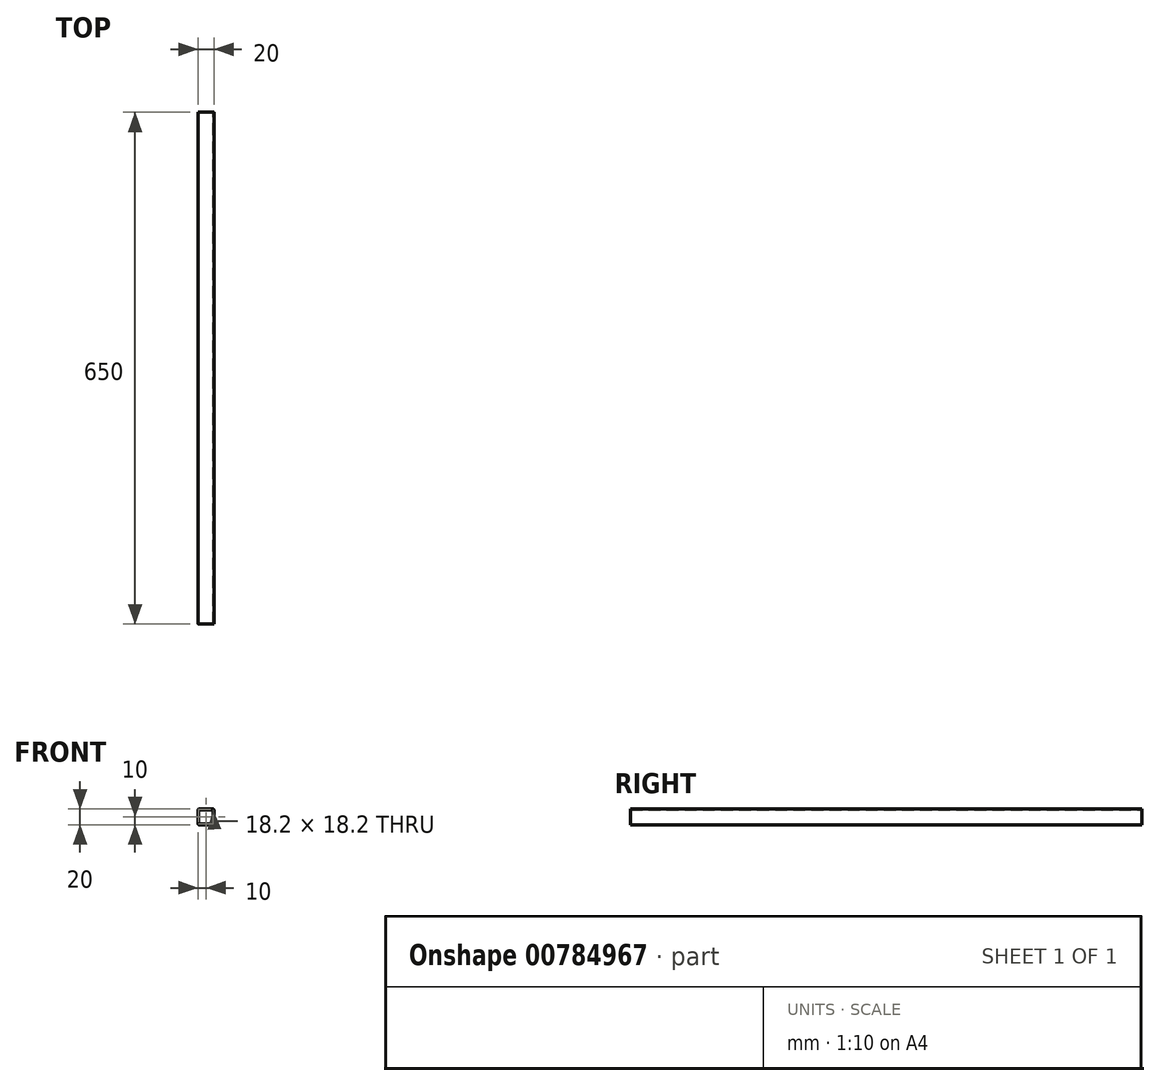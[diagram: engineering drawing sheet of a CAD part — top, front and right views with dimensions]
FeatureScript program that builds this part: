
annotation { "Feature Type Name" : "Feature", "Feature Type Description" : "" }
export const myFeature = defineFeature(function(context is Context, id is Id, definition is map)
    precondition{}
    {
        {
            var Q0;
            Q0=qCreatedBy(makeId("Front.planeOp"),FACE);
            var sketch = newSketch(context, id + "F0", { "sketchPlane" : qUnion([Q0])});
            skLineSegment(sketch, "E0.bottom", {"start": v(-10, 10) * mm, "end": v(10, 10) * mm});
            skLineSegment(sketch, "E0.top", {"start": v(-10, -10) * mm, "end": v(10, -10) * mm});
            skLineSegment(sketch, "E0.left", {"start": v(-10, 10) * mm, "end": v(-10, -10) * mm});
            skLineSegment(sketch, "E0.right", {"start": v(10, 10) * mm, "end": v(10, -10) * mm});
            skPoint(sketch, "E0.middle", {"position": v(0, 0) * mm});
            skLineSegment(sketch, "E1.0", {"start": v(-9.1, 9.1) * mm, "end": v(9.1, 9.1) * mm});
            skLineSegment(sketch, "E1.1", {"start": v(-9.1, 9.1) * mm, "end": v(-9.1, -9.1) * mm});
            skLineSegment(sketch, "E1.2", {"start": v(-9.1, -9.1) * mm, "end": v(9.1, -9.1) * mm});
            skLineSegment(sketch, "E1.3", {"start": v(9.1, 9.1) * mm, "end": v(9.1, -9.1) * mm});
            skSolve(sketch);
        }
        {
            var Q0;
            Q0=makeQuery(id+"F0.imprint","IMPRINT",FACE,{"disambiguationData":[TD([[makeQuery(id+"F0.imprint","IMPRINT",EDGE,{"derivedFrom":sQuery(id+"F0.wireOp",EDGE,"E0.bottom")}),-1.0]])]});
            extrude(context, id + "F1", {"entities" : qUnion([Q0]), "endBound" : BoundingType.SYMMETRIC, "depth" : 650 * mm, "offsetDistance" : 25 * mm});
        }
        {
            var Q0;
            Q0=makeQuery(id+"F1.opExtrude","SWEPT_EDGE",EDGE,{"disambiguationData":[OSD([sQuery(id+"F0.wireOp",EDGE,"E0.bottom"),sQuery(id+"F0.wireOp",EDGE,"E0.right")])]});
            var Q1;
            Q1=makeQuery(id+"F1.opExtrude","SWEPT_EDGE",EDGE,{"disambiguationData":[OSD([sQuery(id+"F0.wireOp",EDGE,"E0.bottom"),sQuery(id+"F0.wireOp",EDGE,"E0.left")])]});
            var Q2;
            Q2=makeQuery(id+"F1.opExtrude","SWEPT_EDGE",EDGE,{"disambiguationData":[OSD([sQuery(id+"F0.wireOp",EDGE,"E0.top"),sQuery(id+"F0.wireOp",EDGE,"E0.right")])]});
            var Q3;
            Q3=makeQuery(id+"F1.opExtrude","SWEPT_EDGE",EDGE,{"disambiguationData":[OSD([sQuery(id+"F0.wireOp",EDGE,"E0.top"),sQuery(id+"F0.wireOp",EDGE,"E0.left")])]});
            fillet(context, id + "F2", {"entities" : qUnion([Q0, Q1, Q2, Q3]), "radius" : 1 * mm, "tangentPropagation" : true, "allowEdgeOverflow" : false});
        }
    });
